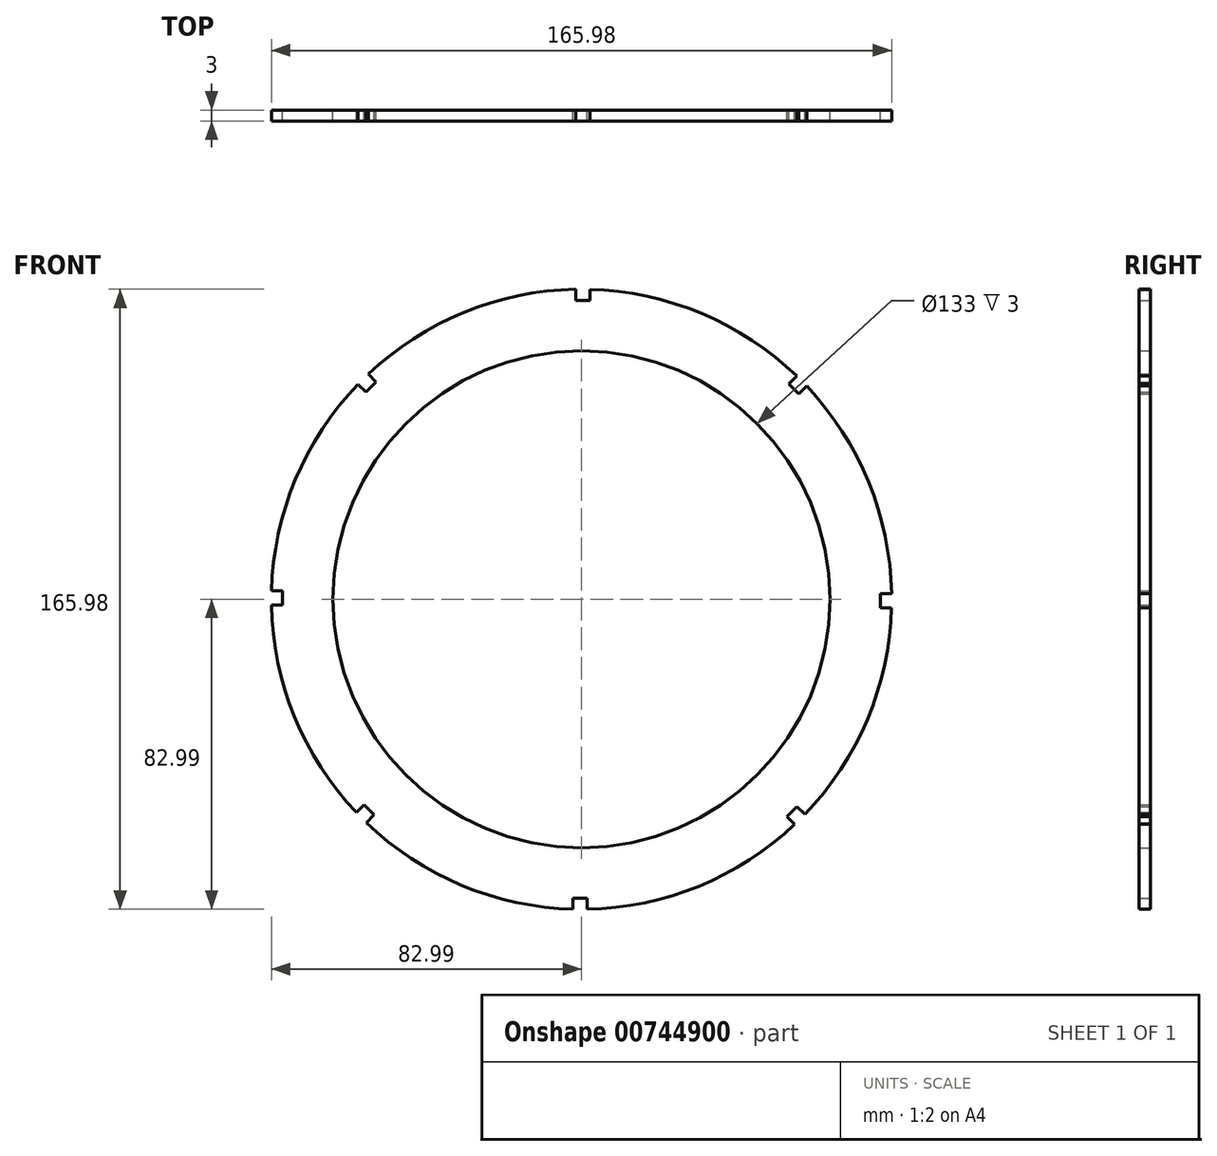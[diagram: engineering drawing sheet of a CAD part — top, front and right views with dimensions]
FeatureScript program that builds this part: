
annotation { "Feature Type Name" : "Feature", "Feature Type Description" : "" }
export const myFeature = defineFeature(function(context is Context, id is Id, definition is map)
    precondition{}
    {
        {
            var Q0;
            Q0=qCreatedBy(makeId("Front.planeOp"),FACE);
            var sketch = newSketch(context, id + "F0", { "sketchPlane" : qUnion([Q0])});
            skCircle(sketch, "E0", {"center": v(0, 0) * mm, "radius": 83 * mm});
            skCircle(sketch, "E1", {"center": v(0, 0) * mm, "radius": 66.5 * mm});
            skLineSegment(sketch, "E2.bottom", {"start": v(-1.55, 84.5) * mm, "end": v(2.25, 84.5) * mm});
            skLineSegment(sketch, "E2.top", {"start": v(-1.55, 80) * mm, "end": v(2.25, 80) * mm});
            skLineSegment(sketch, "E2.left", {"start": v(-1.55, 84.5) * mm, "end": v(-1.55, 80) * mm});
            skLineSegment(sketch, "E2.right", {"start": v(2.25, 84.5) * mm, "end": v(2.25, 80) * mm});
            skLineSegment(sketch, "E3.1.0", {"start": v(-57.66, 55.47) * mm, "end": v(-54.98, 58.16) * mm});
            skLineSegment(sketch, "E3.1.1", {"start": v(-58.16, 61.34) * mm, "end": v(-54.98, 58.16) * mm});
            skLineSegment(sketch, "E3.1.2", {"start": v(-60.85, 58.65) * mm, "end": v(-58.16, 61.34) * mm});
            skLineSegment(sketch, "E3.1.3", {"start": v(-60.85, 58.65) * mm, "end": v(-57.66, 55.47) * mm});
            skLineSegment(sketch, "E3.2.0", {"start": v(-80, -1.55) * mm, "end": v(-80, 2.25) * mm});
            skLineSegment(sketch, "E3.2.1", {"start": v(-84.5, 2.25) * mm, "end": v(-80, 2.25) * mm});
            skLineSegment(sketch, "E3.2.2", {"start": v(-84.5, -1.55) * mm, "end": v(-84.5, 2.25) * mm});
            skLineSegment(sketch, "E3.2.3", {"start": v(-84.5, -1.55) * mm, "end": v(-80, -1.55) * mm});
            skLineSegment(sketch, "E3.3.0", {"start": v(-55.47, -57.66) * mm, "end": v(-58.16, -54.98) * mm});
            skLineSegment(sketch, "E3.3.1", {"start": v(-61.34, -58.16) * mm, "end": v(-58.16, -54.98) * mm});
            skLineSegment(sketch, "E3.3.2", {"start": v(-58.65, -60.85) * mm, "end": v(-61.34, -58.16) * mm});
            skLineSegment(sketch, "E3.3.3", {"start": v(-58.65, -60.85) * mm, "end": v(-55.47, -57.66) * mm});
            skLineSegment(sketch, "E3.4.0", {"start": v(1.55, -80) * mm, "end": v(-2.25, -80) * mm});
            skLineSegment(sketch, "E3.4.1", {"start": v(-2.25, -84.5) * mm, "end": v(-2.25, -80) * mm});
            skLineSegment(sketch, "E3.4.2", {"start": v(1.55, -84.5) * mm, "end": v(-2.25, -84.5) * mm});
            skLineSegment(sketch, "E3.4.3", {"start": v(1.55, -84.5) * mm, "end": v(1.55, -80) * mm});
            skLineSegment(sketch, "E3.5.0", {"start": v(57.66, -55.47) * mm, "end": v(54.98, -58.16) * mm});
            skLineSegment(sketch, "E3.5.1", {"start": v(58.16, -61.34) * mm, "end": v(54.98, -58.16) * mm});
            skLineSegment(sketch, "E3.5.2", {"start": v(60.85, -58.65) * mm, "end": v(58.16, -61.34) * mm});
            skLineSegment(sketch, "E3.5.3", {"start": v(60.85, -58.65) * mm, "end": v(57.66, -55.47) * mm});
            skLineSegment(sketch, "E3.6.0", {"start": v(80, 1.55) * mm, "end": v(80, -2.25) * mm});
            skLineSegment(sketch, "E3.6.1", {"start": v(84.5, -2.25) * mm, "end": v(80, -2.25) * mm});
            skLineSegment(sketch, "E3.6.2", {"start": v(84.5, 1.55) * mm, "end": v(84.5, -2.25) * mm});
            skLineSegment(sketch, "E3.6.3", {"start": v(84.5, 1.55) * mm, "end": v(80, 1.55) * mm});
            skLineSegment(sketch, "E3.7.0", {"start": v(55.47, 57.66) * mm, "end": v(58.16, 54.98) * mm});
            skLineSegment(sketch, "E3.7.1", {"start": v(61.34, 58.16) * mm, "end": v(58.16, 54.98) * mm});
            skLineSegment(sketch, "E3.7.2", {"start": v(58.65, 60.85) * mm, "end": v(61.34, 58.16) * mm});
            skLineSegment(sketch, "E3.7.3", {"start": v(58.65, 60.85) * mm, "end": v(55.47, 57.66) * mm});
            skSolve(sketch);
        }
        {
            var Q0;
            Q0=makeQuery(id+"F0.imprint","IMPRINT",FACE,{"disambiguationData":[TD([[makeQuery(id+"F0.imprint","IMPRINT",EDGE,{"derivedFrom":sQuery(id+"F0.wireOp",EDGE,"E1")}),-1.0]])]});
            extrude(context, id + "F1", {"entities" : qUnion([Q0]), "depth" : 3 * mm, "offsetDistance" : 25 * mm});
        }
    });
